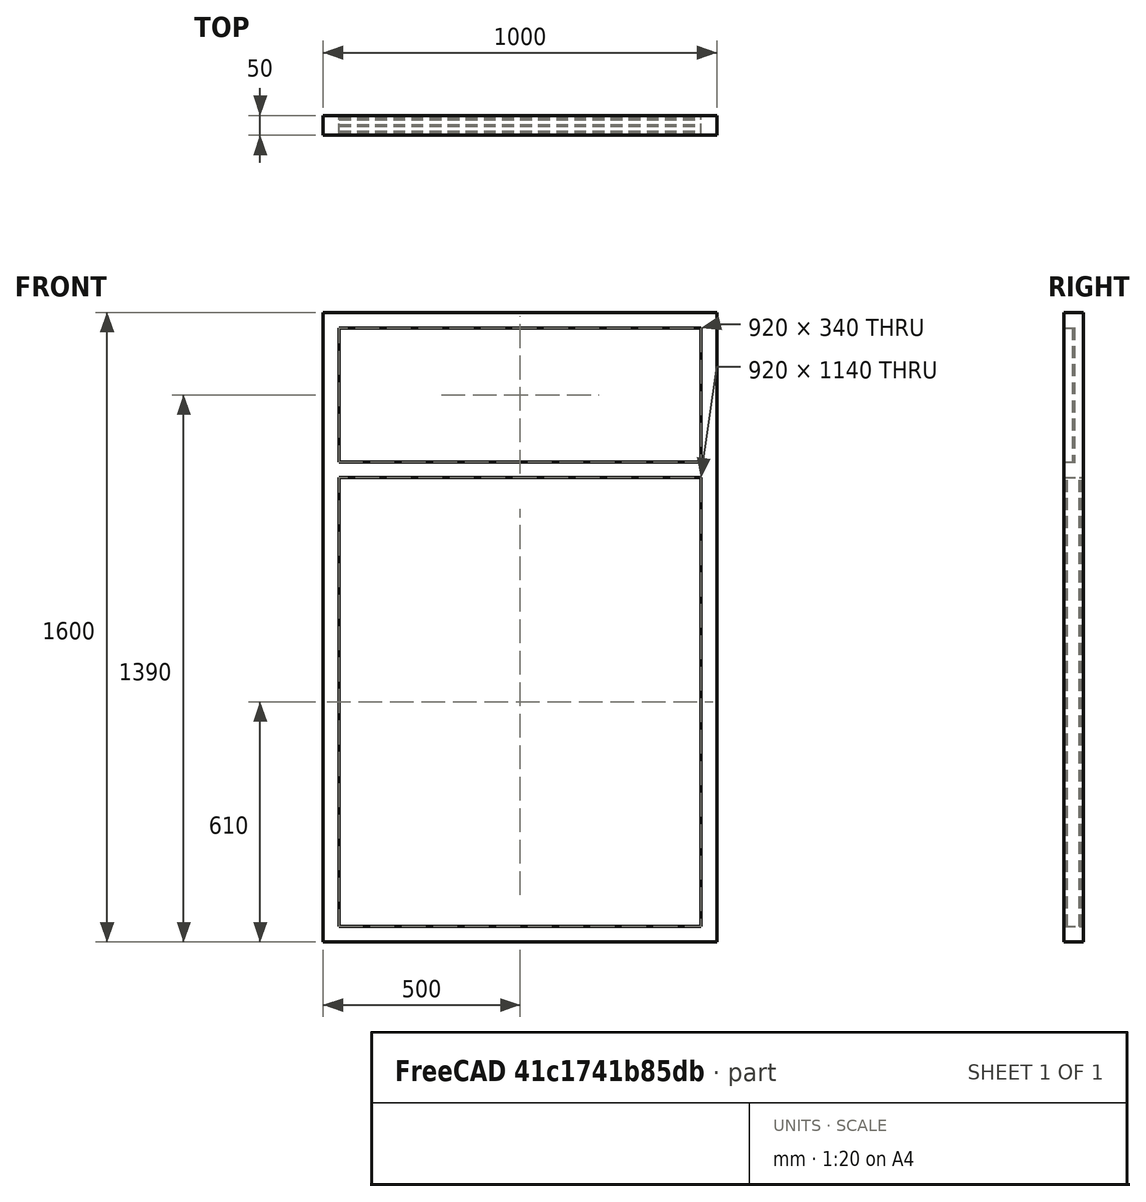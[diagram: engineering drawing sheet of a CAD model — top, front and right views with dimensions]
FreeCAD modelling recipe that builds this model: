
FCSTD DOCUMENT  (FreeCAD 0.16R6704 (Git))
Label: Double glazed window with shutters and simple
License: CreativeCommons Attribution
LicenseURL: http://creativecommons.org/licenses/by/4.0/
objects: Sketcher::SketchObject×2, Part::FeaturePython×2, Part::Extrusion×1, App::DocumentObjectGroup×1
note: 5 computed .brp shape members not serialized (recipe doc carries the construction recipe); baked Part::Feature solids carry a one-line shape summary decoded from their .brp

FEATURE [Sketcher::SketchObject] Sketch094  label="Esboco_janela_fixa_persiana"
  Placement = pos=(0,0,0) rot=(1,0,0;1.5708rad)
  sketch-geometry (18):
    g0: LineSegment StartX=0 StartY=0 StartZ=0 EndX=1000 EndY=0 EndZ=0
    g1: LineSegment StartX=1000 StartY=0 StartZ=0 EndX=1000 EndY=1600 EndZ=0
    g2: LineSegment StartX=1000 StartY=1600 StartZ=0 EndX=0 EndY=1600 EndZ=0
    g3: LineSegment StartX=0 StartY=1600 StartZ=0 EndX=0 EndY=0 EndZ=0
    g4: LineSegment StartX=40 StartY=40 StartZ=0 EndX=960 EndY=40 EndZ=0
    g5: LineSegment StartX=960 StartY=40 StartZ=0 EndX=960 EndY=1180 EndZ=0
    g6: LineSegment StartX=960 StartY=1180 StartZ=0 EndX=40 EndY=1180 EndZ=0
    g7: LineSegment StartX=40 StartY=1180 StartZ=0 EndX=40 EndY=40 EndZ=0
    g8: LineSegment StartX=40 StartY=1560 StartZ=0 EndX=960 EndY=1560 EndZ=0
    g9: LineSegment StartX=960 StartY=1560 StartZ=0 EndX=960 EndY=1220 EndZ=0
    g10: LineSegment StartX=960 StartY=1220 StartZ=0 EndX=40 EndY=1220 EndZ=0
    g11: LineSegment StartX=40 StartY=1220 StartZ=0 EndX=40 EndY=1560 EndZ=0
    g12: LineSegment [constr] StartX=-307.315 StartY=1200 StartZ=0 EndX=1727 EndY=1200 EndZ=0
    g13: LineSegment [constr] StartX=454.414 StartY=1560 StartZ=0 EndX=454.414 EndY=1600 EndZ=0
    g14: LineSegment [constr] StartX=960 StartY=1429.77 StartZ=0 EndX=1000 EndY=1429.77 EndZ=0
    g15: LineSegment [constr] StartX=794.382 StartY=1220 StartZ=0 EndX=794.382 EndY=1180 EndZ=0
    g16: LineSegment [constr] StartX=416.782 StartY=40 StartZ=0 EndX=416.782 EndY=0 EndZ=0
    g17: LineSegment [constr] StartX=0 StartY=1343.77 StartZ=0 EndX=40 EndY=1343.77 EndZ=0
  constraints (52):
    c: Coincident(g0,g1)
    c: Coincident(g1,g2)
    c: Coincident(g2,g3)
    c: Coincident(g3,g0)
    c: Horizontal(g0)
    c: Horizontal(g2)
    c: Vertical(g1)
    c: Vertical(g3)
    c: Coincident(g4,g5)
    c: Coincident(g5,g6)
    c: Coincident(g6,g7)
    c: Coincident(g7,g4)
    c: Horizontal(g4)
    c: Horizontal(g6)
    c: Vertical(g5)
    c: Vertical(g7)
    c: DistanceX(g0) = 1000  'Largura_vao'
    c: Coincident(g0,g-1)
    c: Coincident(g8,g9)
    c: Coincident(g9,g10)
    c: Coincident(g10,g11)
    c: Coincident(g11,g8)
    c: Horizontal(g8)
    c: Horizontal(g10)
    c: Vertical(g9)
    c: Vertical(g11)
    c: DistanceX(g2,g8) = 40  'Perfil_montantes'
    c: DistanceX(g9,g5) = 0  'Constraint29'
    c: Horizontal(g12)
    c: Symmetric(g9,g5,g12)
    c: DistanceY(g0,g1) = 1600  'Altura_vao'
    c: DistanceY(g0,g12) = 1200  'Altura_eixo_janela_inferior'
    c: PointOnObject(g13,g2)  'Constraint36'
    c: PointOnObject(g13,g8)  'Constraint34'
    c: PointOnObject(g14,g9)
    c: PointOnObject(g14,g1)
    c: PointOnObject(g15,g10)
    c: PointOnObject(g15,g6)
    c: PointOnObject(g16,g4)
    c: PointOnObject(g16,g0)
    c: PointOnObject(g17,g3)
    c: PointOnObject(g17,g11)
    c: DistanceX(g10,g6) = 0
    c: Equal(g13,g17)
    c: Equal(g17,g15)
    c: Equal(g15,g14)
    c: Equal(g14,g16)
    c: Angle(g13) = 1.5708
    c: Angle(g17) = 0
    c: Angle(g14) = 0
    c: Angle(g15) = -1.5708
    c: Angle(g16) = -1.5708
FEATURE [Part::FeaturePython] Window073  label="Double glazed window with shutters and simple "  # WARN: FeaturePython — macro-defined, semantics opaque (R4)
  Base = -> Sketch094
  Height = 1000
  HoleDepth = 0
  MoveWithHost = true
  Normal = (0,1,0)
  Preset = 1
  Role = 0
  Width = 1000
  WindowParts = MONTANTES | Frame | Wire0,Wire1,Wire2 | 50.0 | 0.0 | VIDRO SUPERIOR | Glass panel | Wire1 | 5.0 | 5.0 | VIDRO 1 | Glass panel | Wire1 | 5.0 | 40.0 | VIDRO 2 | Glass panel | Wire2 | 5.0 | 22.5
FEATURE [Sketcher::SketchObject] Sketch095
  ExternalGeometry = -> [Window073]
  Placement = pos=(40,0,0) rot=(0.57735,0.57735,0.57735;2.0944rad)
  Support = -> Window073 [Face12]
  sketch-geometry (3):
    g0: ArcOfCircle CenterX=25 CenterY=1172 CenterZ=0 NormalX=0 NormalY=0 NormalZ=1 Radius=7 StartAngle=4.71239 EndAngle=7.85398
    g1: LineSegment [constr] StartX=25 StartY=-16508.7 StartZ=0 EndX=25 EndY=-8.54422 EndZ=0
    g2: ArcOfCircle CenterX=25 CenterY=1158 CenterZ=0 NormalX=0 NormalY=0 NormalZ=1 Radius=7 StartAngle=1.5708 EndAngle=4.71239
  constraints (10):
    c: Coincident(g0,g2)
    c: PointOnObject(g0,g1)
    c: PointOnObject(g0,g1)
    c: PointOnObject(g0,g1)
    c: PointOnObject(g2,g1)
    c: PointOnObject(g2,g1)
    c: Symmetric(g-4,g-4,g1)
    c: DistanceY(g0,g-4) = 1
    c: DistanceY(g0,g0) = 14
    c: DistanceY(g2,g0) = 14
FEATURE [Part::Extrusion] Extrude_Sketch094  label="Módulo persiana"
  Base = -> Sketch095
  Dir = (920,0,0)
  Solid = true
  expr: Dir.x = Esboco_janela_fixa_persiana.Constraints.Largura_vao - 2 * Esboco_janela_fixa_persiana.Constraints.Perfil_montantes
FEATURE [Part::FeaturePython] Array  label="Internal blind"  # Draft array (typed FeaturePython)
  Angle = 360
  ArrayType = 0
  Axis = (0,0,1)
  Base = -> Extrude_Sketch094
  Center = (0,0,0)
  Fuse = false
  IntervalAxis = (0,0,0)
  IntervalX = (1,0,0)
  IntervalY = (0,1,0)
  IntervalZ = (0,0,-28)
  NumberPolar = 1
  NumberX = 1
  NumberY = 1
  NumberZ = 40
  expr: NumberZ = (Esboco_janela_fixa_persiana.Constraints.Altura_eixo_janela_inferior - 2 * Esboco_janela_fixa_persiana.Constraints.Perfil_montantes) / 28
FEATURE [App::DocumentObjectGroup] Grupo081  label="Double glazed window with shutters and simple"
  Group = -> [Window073,Extrude_Sketch094,Array]
